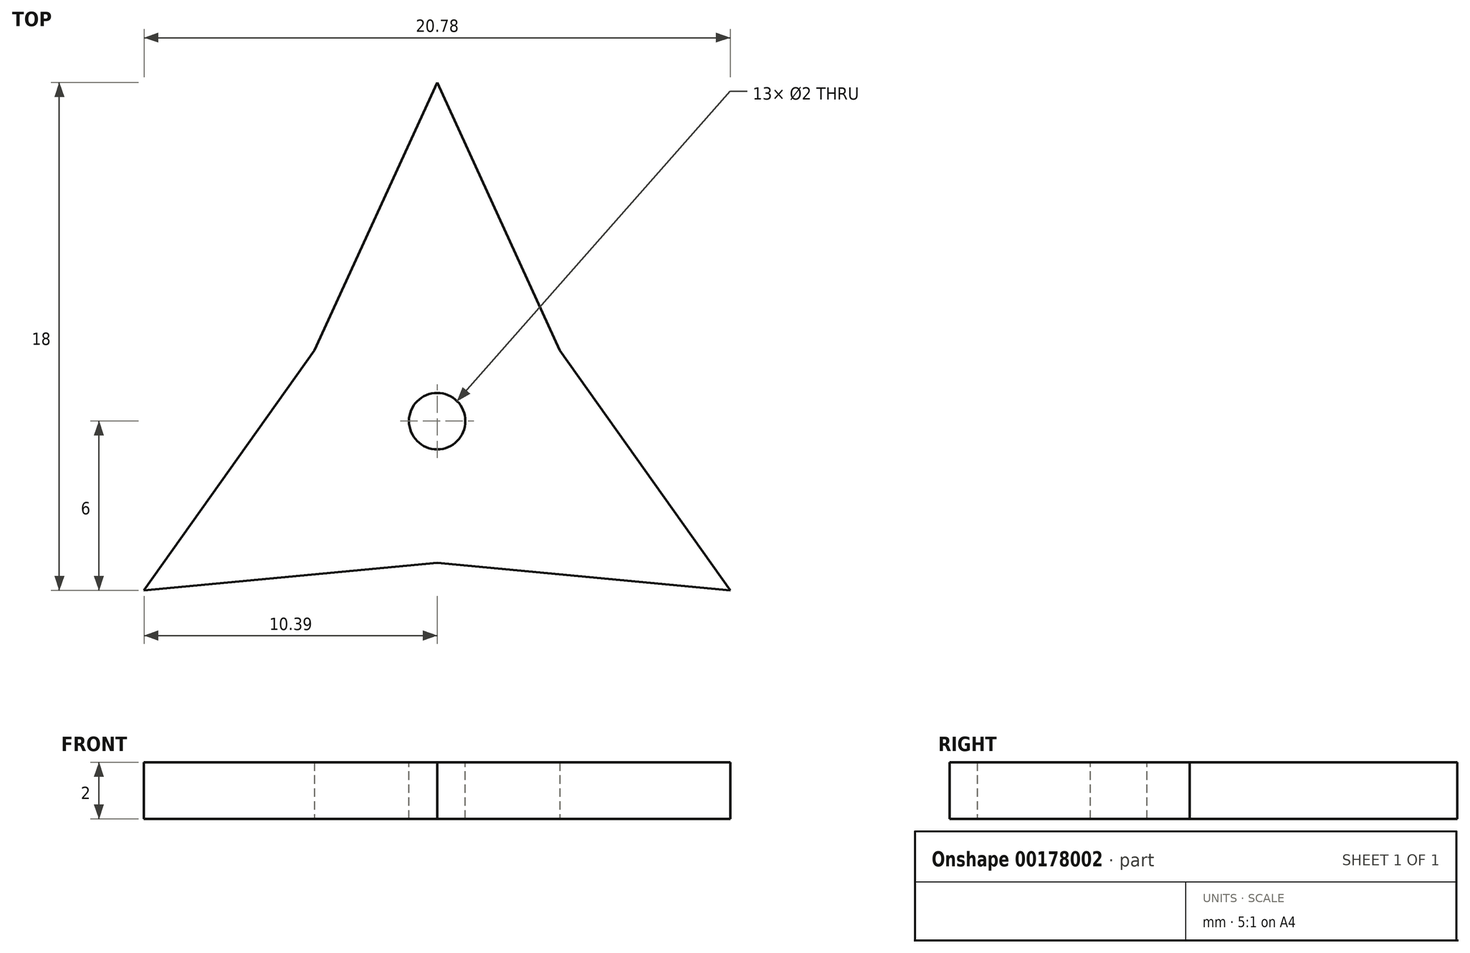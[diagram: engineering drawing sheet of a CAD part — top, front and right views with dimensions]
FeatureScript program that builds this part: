
annotation { "Feature Type Name" : "Feature", "Feature Type Description" : "" }
export const myFeature = defineFeature(function(context is Context, id is Id, definition is map)
    precondition{}
    {
        {
            var Q0;
            Q0=qCreatedBy(makeId("Top.planeOp"),FACE);
            var sketch = newSketch(context, id + "F0", { "sketchPlane" : qUnion([Q0])});
            skCircle(sketch, "E0", {"center": v(0, 0) * mm, "radius": 5 * mm});
            skLineSegment(sketch, "E1", {"start": v(0, 0) * mm, "end": v(0, 5) * mm, "construction": true});
            skLineSegment(sketch, "E2", {"start": v(0, 12) * mm, "end": v(-4.55, 2.08) * mm});
            skLineSegment(sketch, "E3.MirrorCS", {"start": v(0, 12) * mm, "end": v(4.55, 2.08) * mm});
            skLineSegment(sketch, "E4.1.0", {"start": v(-10.4, -6) * mm, "end": v(0.47, -4.98) * mm});
            skLineSegment(sketch, "E4.1.1", {"start": v(-10.4, -6) * mm, "end": v(-4.08, 2.9) * mm});
            skLineSegment(sketch, "E4.2.0", {"start": v(10.4, -6) * mm, "end": v(4.08, 2.9) * mm});
            skLineSegment(sketch, "E4.2.1", {"start": v(10.4, -6) * mm, "end": v(-0.47, -4.98) * mm});
            skSolve(sketch);
        }
        {
            var Q0;
            Q0 = qSketchRegion(id + "F0", true);
            var Q1;
            {var subQ0=sQuery(id+"F0.wireOp",EDGE,"E0");var subQ5=makeQuery(id+"F0.imprint","INTERSECT",VERTEX,{"derivedFrom":[subQ0,sQuery(id+"F0.wireOp",EDGE,"E3.MirrorCS")]});Q1=makeQuery(id+"F0.imprint","IMPRINT",FACE,{"disambiguationData":[TD([[makeQuery(id+"F0.imprint","IMPRINT",EDGE,{"disambiguationData":[TD([[subQ5,-1.0]])],"derivedFrom":subQ0}),1.0]])]});}
            extrude(context, id + "F1", {"entities" : qUnion([Q0, Q1]), "depth" : 2 * mm});
        }
        {
            var Q0;
            Q0=makeQuery(id+"F1.opExtrude","CAP_FACE",FACE,{"disambiguationData":[OSD([sQuery(id+"F0.wireOp",EDGE,"E2"),sQuery(id+"F0.wireOp",EDGE,"E3.MirrorCS"),sQuery(id+"F0.wireOp",EDGE,"E4.1.0"),sQuery(id+"F0.wireOp",EDGE,"E4.1.1"),sQuery(id+"F0.wireOp",EDGE,"E4.2.0"),sQuery(id+"F0.wireOp",EDGE,"E4.2.1")])],"isStart":false});
            var sketch = newSketch(context, id + "F2", { "sketchPlane" : qUnion([Q0])});
            skCircle(sketch, "E5", {"center": v(0, 0) * mm, "radius": 1 * mm});
            skSolve(sketch);
        }
        {
            var Q0;
            Q0 = qSketchRegion(id + "F2", true);
            extrude(context, id + "F3", {"entities" : qUnion([Q0]), "operationType" : NewBodyOperationType.REMOVE, "endBound" : BoundingType.THROUGH_ALL, "oppositeDirection" : true, "depth" : 25 * mm});
        }
    });
